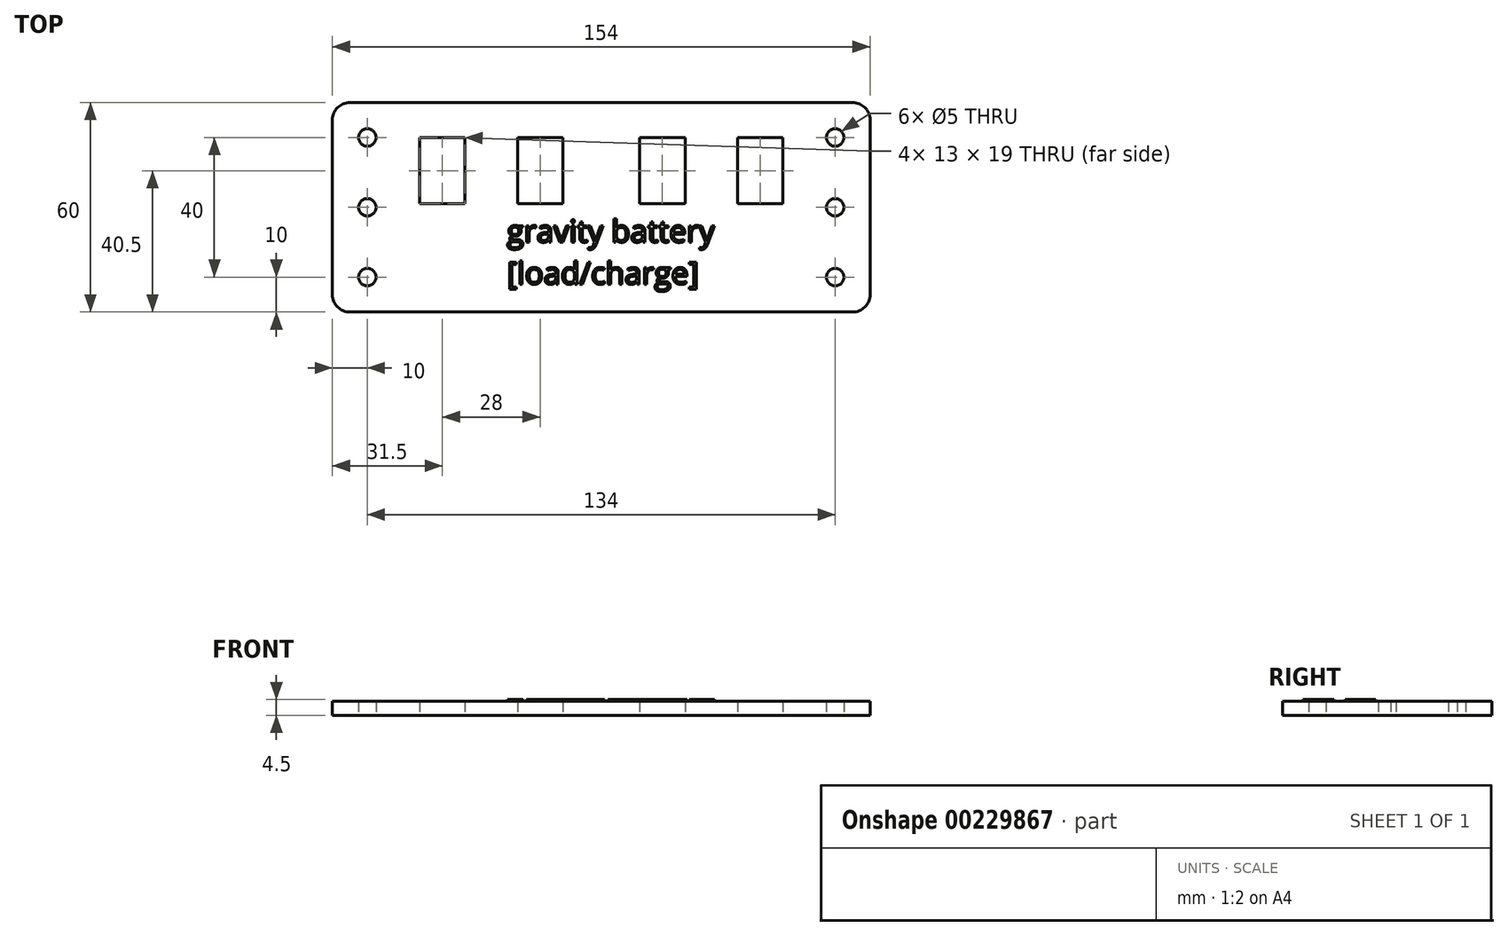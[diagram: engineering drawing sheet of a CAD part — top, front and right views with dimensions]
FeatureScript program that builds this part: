
annotation { "Feature Type Name" : "Feature", "Feature Type Description" : "" }
export const myFeature = defineFeature(function(context is Context, id is Id, definition is map)
    precondition{}
    {
        {
            var Q0;
            Q0=qCreatedBy(makeId("Top.planeOp"),FACE);
            var sketch = newSketch(context, id + "F0", { "sketchPlane" : qUnion([Q0])});
            skPoint(sketch, "E0", {"position": v(-0.2, -0.3) * mm});
            skLineSegment(sketch, "E1.right", {"start": v(-77.2, -10.3) * mm, "end": v(-77.2, 9.7) * mm});
            skLineSegment(sketch, "E2.right", {"start": v(76.8, 9.7) * mm, "end": v(76.8, -10.3) * mm});
            skPoint(sketch, "E3", {"position": v(-67.2, -0.3) * mm});
            skPoint(sketch, "E3.positionSnap0", {"position": v(-57.2, 0.7) * mm});
            skPoint(sketch, "E3.positionSnap1", {"position": v(-67.2, 9.7) * mm});
            skPoint(sketch, "E4", {"position": v(66.8, -0.3) * mm});
            skPoint(sketch, "E4.positionSnap0", {"position": v(56.8, -0.3) * mm});
            skPoint(sketch, "E4.positionSnap1", {"position": v(66.8, 9.7) * mm});
            skCircle(sketch, "E5", {"center": v(-67.2, -0.3) * mm, "radius": 2.5 * mm});
            skCircle(sketch, "E6", {"center": v(66.8, -0.3) * mm, "radius": 2.5 * mm});
            skLineSegment(sketch, "E7.top", {"start": v(-72.2, 29.7) * mm, "end": v(-62.2, 29.7) * mm});
            skLineSegment(sketch, "E7.left", {"start": v(-77.2, 9.7) * mm, "end": v(-77.2, 24.7) * mm});
            skLineSegment(sketch, "E8.top", {"start": v(-72.2, -30.3) * mm, "end": v(-62.2, -30.3) * mm});
            skLineSegment(sketch, "E8.left", {"start": v(-77.2, -10.3) * mm, "end": v(-77.2, -25.3) * mm});
            skLineSegment(sketch, "E9.top", {"start": v(61.8, 29.7) * mm, "end": v(71.8, 29.7) * mm});
            skLineSegment(sketch, "E9.right", {"start": v(76.8, 9.7) * mm, "end": v(76.8, 24.7) * mm});
            skLineSegment(sketch, "E10.top", {"start": v(61.8, -30.3) * mm, "end": v(71.8, -30.3) * mm});
            skLineSegment(sketch, "E10.right", {"start": v(76.8, -10.3) * mm, "end": v(76.8, -25.3) * mm});
            skPoint(sketch, "E11.positionSnap0", {"position": v(-52.2, 19.7) * mm});
            skPoint(sketch, "E11.positionSnap1", {"position": v(-64.7, 29.7) * mm});
            skPoint(sketch, "E12", {"position": v(66.8, 19.7) * mm});
            skPoint(sketch, "E12.positionSnap0", {"position": v(66.8, 29.7) * mm});
            skPoint(sketch, "E12.positionSnap1", {"position": v(76.8, 19.7) * mm});
            skPoint(sketch, "E13", {"position": v(66.8, -20.3) * mm});
            skPoint(sketch, "E13.positionSnap0", {"position": v(76.8, -20.3) * mm});
            skPoint(sketch, "E13.positionSnap1", {"position": v(66.8, -30.3) * mm});
            skPoint(sketch, "E14", {"position": v(-67.2, -20.3) * mm});
            skPoint(sketch, "E14.positionSnap0", {"position": v(-77.2, -20.3) * mm});
            skPoint(sketch, "E14.positionSnap1", {"position": v(-67.2, -30.3) * mm});
            skCircle(sketch, "E15", {"center": v(66.8, 19.7) * mm, "radius": 2.5 * mm});
            skCircle(sketch, "E16", {"center": v(66.8, -20.3) * mm, "radius": 2.5 * mm});
            skCircle(sketch, "E17", {"center": v(-67.2, -20.3) * mm, "radius": 2.5 * mm});
            skPoint(sketch, "E18.visualSharp", {"position": v(-52.2, 9.7) * mm});
            skPoint(sketch, "E19.visualSharp", {"position": v(-57.2, -38.58) * mm});
            skPoint(sketch, "E20.visualSharp", {"position": v(2.8, -10.3) * mm});
            skPoint(sketch, "E21.visualSharp", {"position": v(56.8, 9.7) * mm});
            skPoint(sketch, "E22.visualSharp", {"position": v(56.8, 29.7) * mm});
            skPoint(sketch, "E23.visualSharp", {"position": v(76.8, 29.7) * mm});
            skArc(sketch, "E23.filletArc", {"start": v(76.8, 24.7) * mm, "mid": v(75.34, 28.24) * mm, "end": v(71.8, 29.7) * mm});
            skPoint(sketch, "E24.visualSharp", {"position": v(56.8, -30.3) * mm});
            skPoint(sketch, "E25.visualSharp", {"position": v(76.8, -30.3) * mm});
            skArc(sketch, "E25.filletArc", {"start": v(71.8, -30.3) * mm, "mid": v(75.34, -28.84) * mm, "end": v(76.8, -25.3) * mm});
            skPoint(sketch, "E26.visualSharp", {"position": v(-57.2, -30.3) * mm});
            skPoint(sketch, "E27.visualSharp", {"position": v(-77.2, -30.3) * mm});
            skArc(sketch, "E27.filletArc", {"start": v(-77.2, -25.3) * mm, "mid": v(-75.74, -28.84) * mm, "end": v(-72.2, -30.3) * mm});
            skPoint(sketch, "E28.visualSharp", {"position": v(-77.2, 29.7) * mm});
            skArc(sketch, "E28.filletArc", {"start": v(-72.2, 29.7) * mm, "mid": v(-75.74, 28.24) * mm, "end": v(-77.2, 24.7) * mm});
            skPoint(sketch, "E29.visualSharp", {"position": v(-52.2, 29.7) * mm});
            skLineSegment(sketch, "E30.left", {"start": v(-77.2, 24.7) * mm, "end": v(-77.2, -20.3) * mm});
            skLineSegment(sketch, "E31.left", {"start": v(76.8, 24.7) * mm, "end": v(76.8, -25.3) * mm});
            skLineSegment(sketch, "E32", {"start": v(-62.2, 29.7) * mm, "end": v(61.8, 29.7) * mm});
            skLineSegment(sketch, "E33", {"start": v(-62.2, -30.3) * mm, "end": v(61.8, -30.3) * mm});
            skLineSegment(sketch, "E34.bottom", {"start": v(-52.2, 19.7) * mm, "end": v(-39.2, 19.7) * mm});
            skLineSegment(sketch, "E34.top", {"start": v(-52.2, 0.7) * mm, "end": v(-39.2, 0.7) * mm});
            skLineSegment(sketch, "E34.left", {"start": v(-52.2, 19.7) * mm, "end": v(-52.2, 0.7) * mm});
            skLineSegment(sketch, "E34.right", {"start": v(-39.2, 19.7) * mm, "end": v(-39.2, 0.7) * mm});
            skLineSegment(sketch, "E35.bottom", {"start": v(-24.2, 19.7) * mm, "end": v(-11.2, 19.7) * mm});
            skLineSegment(sketch, "E35.top", {"start": v(-24.2, 0.7) * mm, "end": v(-11.2, 0.7) * mm});
            skLineSegment(sketch, "E35.left", {"start": v(-24.2, 19.7) * mm, "end": v(-24.2, 0.7) * mm});
            skLineSegment(sketch, "E35.right", {"start": v(-11.2, 19.7) * mm, "end": v(-11.2, 0.7) * mm});
            skLineSegment(sketch, "E36.bottom", {"start": v(10.8, 19.7) * mm, "end": v(23.8, 19.7) * mm});
            skLineSegment(sketch, "E36.top", {"start": v(10.8, 0.7) * mm, "end": v(23.8, 0.7) * mm});
            skLineSegment(sketch, "E36.left", {"start": v(10.8, 19.7) * mm, "end": v(10.8, 0.7) * mm});
            skLineSegment(sketch, "E36.right", {"start": v(23.8, 19.7) * mm, "end": v(23.8, 0.7) * mm});
            skLineSegment(sketch, "E37.bottom", {"start": v(38.8, 19.7) * mm, "end": v(51.8, 19.7) * mm});
            skLineSegment(sketch, "E37.top", {"start": v(38.8, 0.7) * mm, "end": v(51.8, 0.7) * mm});
            skLineSegment(sketch, "E37.left", {"start": v(38.8, 19.7) * mm, "end": v(38.8, 0.7) * mm});
            skLineSegment(sketch, "E37.right", {"start": v(51.8, 19.7) * mm, "end": v(51.8, 0.7) * mm});
            skCircle(sketch, "E38", {"center": v(-67.2, 19.7) * mm, "radius": 2.5 * mm});
            skLineSegment(sketch, "E39", {"start": v(-57.2, 0.7) * mm, "end": v(-57.2, -38.58) * mm, "construction": true});
            skPoint(sketch, "E40", {"position": v(-57.2, -18.94) * mm});
            skLineSegment(sketch, "E41.left", {"start": v(-57.2, -18.94) * mm, "end": v(-57.2, -25.3) * mm});
            skLineSegment(sketch, "E41.right", {"start": v(2.8, -18.94) * mm, "end": v(2.8, -25.3) * mm});
            skText(sketch, "E42", { "text": "gravity battery \n[load/charge]", "fontName": "OpenSans-Regular.ttf"});
            skLineSegment(sketch, "E43.0", {"start": v(-54.2, 21.7) * mm, "end": v(-37.2, 21.7) * mm});
            skLineSegment(sketch, "E43.1", {"start": v(-54.2, 21.7) * mm, "end": v(-54.2, -1.3) * mm});
            skLineSegment(sketch, "E43.2", {"start": v(-54.2, -1.3) * mm, "end": v(-37.2, -1.3) * mm});
            skLineSegment(sketch, "E43.3", {"start": v(-37.2, 21.7) * mm, "end": v(-37.2, -1.3) * mm});
            skLineSegment(sketch, "E44.0", {"start": v(-26.2, 21.7) * mm, "end": v(-9.2, 21.7) * mm});
            skLineSegment(sketch, "E44.1", {"start": v(-26.2, 21.7) * mm, "end": v(-26.2, -1.3) * mm});
            skLineSegment(sketch, "E44.2", {"start": v(-26.2, -1.3) * mm, "end": v(-9.2, -1.3) * mm});
            skLineSegment(sketch, "E44.3", {"start": v(-9.2, 21.7) * mm, "end": v(-9.2, -1.3) * mm});
            skLineSegment(sketch, "E45.0", {"start": v(25.8, 21.7) * mm, "end": v(25.8, -1.3) * mm});
            skLineSegment(sketch, "E45.1", {"start": v(8.8, 21.7) * mm, "end": v(25.8, 21.7) * mm});
            skLineSegment(sketch, "E45.2", {"start": v(8.8, 21.7) * mm, "end": v(8.8, -1.3) * mm});
            skLineSegment(sketch, "E45.3", {"start": v(8.8, -1.3) * mm, "end": v(25.8, -1.3) * mm});
            skLineSegment(sketch, "E46.0", {"start": v(36.8, 21.7) * mm, "end": v(36.8, -1.3) * mm});
            skLineSegment(sketch, "E46.1", {"start": v(36.8, 21.7) * mm, "end": v(53.8, 21.7) * mm});
            skLineSegment(sketch, "E46.2", {"start": v(53.8, 21.7) * mm, "end": v(53.8, -1.3) * mm});
            skLineSegment(sketch, "E46.3", {"start": v(36.8, -1.3) * mm, "end": v(53.8, -1.3) * mm});
            const initialGuessF0  = {"E42": [-0.0272, -0.0103, 1, 0, 0.00636]};
            skSetInitialGuess(sketch, initialGuessF0);
            skSolve(sketch);
        }
        {
            var Q0;
            Q0=makeQuery(id+"F0.imprint","IMPRINT",FACE,{"disambiguationData":[TD([[makeQuery(id+"F0.imprint","IMPRINT",EDGE,{"derivedFrom":sQuery(id+"F0.wireOp",EDGE,"E5")}),-1.0]])]});
            var Q1;
            Q1=makeQuery(id+"F0.imprint","IMPRINT",FACE,{"disambiguationData":[TD([[makeQuery(id+"F0.imprint","IMPRINT",EDGE,{"derivedFrom":sQuery(id+"F0.wireOp",EDGE,"E34.bottom")}),1.0]])]});
            var Q2;
            Q2=makeQuery(id+"F0.imprint","IMPRINT",FACE,{"disambiguationData":[TD([[makeQuery(id+"F0.imprint","IMPRINT",EDGE,{"derivedFrom":sQuery(id+"F0.wireOp",EDGE,"E35.bottom")}),1.0]])]});
            var Q3;
            Q3=makeQuery(id+"F0.imprint","IMPRINT",FACE,{"disambiguationData":[TD([[makeQuery(id+"F0.imprint","IMPRINT",EDGE,{"derivedFrom":sQuery(id+"F0.wireOp",EDGE,"E36.bottom")}),1.0]])]});
            var Q4;
            Q4=makeQuery(id+"F0.imprint","IMPRINT",FACE,{"disambiguationData":[TD([[makeQuery(id+"F0.imprint","IMPRINT",EDGE,{"derivedFrom":sQuery(id+"F0.wireOp",EDGE,"E37.bottom")}),1.0]])]});
            extrude(context, id + "F1", {"entities" : qUnion([Q0, Q1, Q2, Q3, Q4]), "depth" : 4 * mm});
        }
        {
            var Q0;
            Q0=makeQuery(id+"F0.imprint","IMPRINT",FACE,{"disambiguationData":[TD([[makeQuery(id+"F0.imprint","IMPRINT",EDGE,{"derivedFrom":sQuery(id+"F0.wireOp",EDGE,"E42.sketch_text.stroke-285")}),-1.0]])]});
            var Q1;
            Q1=makeQuery(id+"F0.imprint","IMPRINT",FACE,{"disambiguationData":[TD([[makeQuery(id+"F0.imprint","IMPRINT",EDGE,{"derivedFrom":sQuery(id+"F0.wireOp",EDGE,"E42.sketch_text.stroke-277")}),-1.0]])]});
            var Q2;
            Q2=makeQuery(id+"F0.imprint","IMPRINT",FACE,{"disambiguationData":[TD([[makeQuery(id+"F0.imprint","IMPRINT",EDGE,{"derivedFrom":sQuery(id+"F0.wireOp",EDGE,"E42.sketch_text.stroke-289")}),-1.0]])]});
            var Q3;
            Q3=makeQuery(id+"F0.imprint","IMPRINT",FACE,{"disambiguationData":[TD([[makeQuery(id+"F0.imprint","IMPRINT",EDGE,{"derivedFrom":sQuery(id+"F0.wireOp",EDGE,"E42.sketch_text.stroke-306")}),-1.0]])]});
            var Q4;
            Q4=makeQuery(id+"F0.imprint","IMPRINT",FACE,{"disambiguationData":[TD([[makeQuery(id+"F0.imprint","IMPRINT",EDGE,{"derivedFrom":sQuery(id+"F0.wireOp",EDGE,"E42.sketch_text.stroke-333")}),-1.0]])]});
            var Q5;
            Q5=makeQuery(id+"F0.imprint","IMPRINT",FACE,{"disambiguationData":[TD([[makeQuery(id+"F0.imprint","IMPRINT",EDGE,{"derivedFrom":sQuery(id+"F0.wireOp",EDGE,"E42.sketch_text.stroke-357")}),-1.0]])]});
            var Q6;
            Q6=makeQuery(id+"F0.imprint","IMPRINT",FACE,{"disambiguationData":[TD([[makeQuery(id+"F0.imprint","IMPRINT",EDGE,{"derivedFrom":sQuery(id+"F0.wireOp",EDGE,"E42.sketch_text.stroke-361")}),-1.0]])]});
            var Q7;
            Q7=makeQuery(id+"F0.imprint","IMPRINT",FACE,{"disambiguationData":[TD([[makeQuery(id+"F0.imprint","IMPRINT",EDGE,{"derivedFrom":sQuery(id+"F0.wireOp",EDGE,"E42.sketch_text.stroke-376")}),-1.0]])]});
            var Q8;
            Q8=makeQuery(id+"F0.imprint","IMPRINT",FACE,{"disambiguationData":[TD([[makeQuery(id+"F0.imprint","IMPRINT",EDGE,{"derivedFrom":sQuery(id+"F0.wireOp",EDGE,"E42.sketch_text.stroke-394")}),-1.0]])]});
            var Q9;
            Q9=makeQuery(id+"F0.imprint","IMPRINT",FACE,{"disambiguationData":[TD([[makeQuery(id+"F0.imprint","IMPRINT",EDGE,{"derivedFrom":sQuery(id+"F0.wireOp",EDGE,"E42.sketch_text.stroke-421")}),-1.0]])]});
            var Q10;
            Q10=makeQuery(id+"F0.imprint","IMPRINT",FACE,{"disambiguationData":[TD([[makeQuery(id+"F0.imprint","IMPRINT",EDGE,{"derivedFrom":sQuery(id+"F0.wireOp",EDGE,"E42.sketch_text.stroke-434")}),-1.0]])]});
            var Q11;
            Q11=makeQuery(id+"F0.imprint","IMPRINT",FACE,{"disambiguationData":[TD([[makeQuery(id+"F0.imprint","IMPRINT",EDGE,{"derivedFrom":sQuery(id+"F0.wireOp",EDGE,"E42.sketch_text.stroke-478")}),-1.0]])]});
            var Q12;
            Q12=makeQuery(id+"F0.imprint","IMPRINT",FACE,{"disambiguationData":[TD([[makeQuery(id+"F0.imprint","IMPRINT",EDGE,{"derivedFrom":sQuery(id+"F0.wireOp",EDGE,"E42.sketch_text.stroke-497")}),-1.0]])]});
            var Q13;
            Q13=makeQuery(id+"F0.imprint","IMPRINT",FACE,{"disambiguationData":[TD([[makeQuery(id+"F0.imprint","IMPRINT",EDGE,{"derivedFrom":sQuery(id+"F0.wireOp",EDGE,"E42.sketch_text.stroke-0")}),-1.0]])]});
            var Q14;
            Q14=makeQuery(id+"F0.imprint","IMPRINT",FACE,{"disambiguationData":[TD([[makeQuery(id+"F0.imprint","IMPRINT",EDGE,{"derivedFrom":sQuery(id+"F0.wireOp",EDGE,"E42.sketch_text.stroke-44")}),-1.0]])]});
            var Q15;
            Q15=makeQuery(id+"F0.imprint","IMPRINT",FACE,{"disambiguationData":[TD([[makeQuery(id+"F0.imprint","IMPRINT",EDGE,{"derivedFrom":sQuery(id+"F0.wireOp",EDGE,"E42.sketch_text.stroke-57")}),-1.0]])]});
            var Q16;
            Q16=makeQuery(id+"F0.imprint","IMPRINT",FACE,{"disambiguationData":[TD([[makeQuery(id+"F0.imprint","IMPRINT",EDGE,{"derivedFrom":sQuery(id+"F0.wireOp",EDGE,"E42.sketch_text.stroke-84")}),-1.0]])]});
            var Q17;
            Q17=makeQuery(id+"F0.imprint","IMPRINT",FACE,{"disambiguationData":[TD([[makeQuery(id+"F0.imprint","IMPRINT",EDGE,{"derivedFrom":sQuery(id+"F0.wireOp",EDGE,"E42.sketch_text.stroke-94")}),-1.0]])]});
            var Q18;
            Q18=makeQuery(id+"F0.imprint","IMPRINT",FACE,{"disambiguationData":[TD([[makeQuery(id+"F0.imprint","IMPRINT",EDGE,{"derivedFrom":sQuery(id+"F0.wireOp",EDGE,"E42.sketch_text.stroke-98")}),-1.0]])]});
            var Q19;
            Q19=makeQuery(id+"F0.imprint","IMPRINT",FACE,{"disambiguationData":[TD([[makeQuery(id+"F0.imprint","IMPRINT",EDGE,{"derivedFrom":sQuery(id+"F0.wireOp",EDGE,"E42.sketch_text.stroke-106")}),-1.0]])]});
            var Q20;
            Q20=makeQuery(id+"F0.imprint","IMPRINT",FACE,{"disambiguationData":[TD([[makeQuery(id+"F0.imprint","IMPRINT",EDGE,{"derivedFrom":sQuery(id+"F0.wireOp",EDGE,"E42.sketch_text.stroke-125")}),-1.0]])]});
            var Q21;
            Q21=makeQuery(id+"F0.imprint","IMPRINT",FACE,{"disambiguationData":[TD([[makeQuery(id+"F0.imprint","IMPRINT",EDGE,{"derivedFrom":sQuery(id+"F0.wireOp",EDGE,"E42.sketch_text.stroke-141")}),-1.0]])]});
            var Q22;
            Q22=makeQuery(id+"F0.imprint","IMPRINT",FACE,{"disambiguationData":[TD([[makeQuery(id+"F0.imprint","IMPRINT",EDGE,{"derivedFrom":sQuery(id+"F0.wireOp",EDGE,"E42.sketch_text.stroke-164")}),-1.0]])]});
            var Q23;
            Q23=makeQuery(id+"F0.imprint","IMPRINT",FACE,{"disambiguationData":[TD([[makeQuery(id+"F0.imprint","IMPRINT",EDGE,{"derivedFrom":sQuery(id+"F0.wireOp",EDGE,"E42.sketch_text.stroke-191")}),-1.0]])]});
            var Q24;
            Q24=makeQuery(id+"F0.imprint","IMPRINT",FACE,{"disambiguationData":[TD([[makeQuery(id+"F0.imprint","IMPRINT",EDGE,{"derivedFrom":sQuery(id+"F0.wireOp",EDGE,"E42.sketch_text.stroke-210")}),-1.0]])]});
            var Q25;
            Q25=makeQuery(id+"F0.imprint","IMPRINT",FACE,{"disambiguationData":[TD([[makeQuery(id+"F0.imprint","IMPRINT",EDGE,{"derivedFrom":sQuery(id+"F0.wireOp",EDGE,"E42.sketch_text.stroke-229")}),-1.0]])]});
            var Q26;
            Q26=makeQuery(id+"F0.imprint","IMPRINT",FACE,{"disambiguationData":[TD([[makeQuery(id+"F0.imprint","IMPRINT",EDGE,{"derivedFrom":sQuery(id+"F0.wireOp",EDGE,"E42.sketch_text.stroke-248")}),-1.0]])]});
            var Q27;
            Q27=makeQuery(id+"F0.imprint","IMPRINT",FACE,{"disambiguationData":[TD([[makeQuery(id+"F0.imprint","IMPRINT",EDGE,{"derivedFrom":sQuery(id+"F0.wireOp",EDGE,"E42.sketch_text.stroke-261")}),-1.0]])]});
            extrude(context, id + "F2", {"entities" : qUnion([Q0, Q1, Q2, Q3, Q4, Q5, Q6, Q7, Q8, Q9, Q10, Q11, Q12, Q13, Q14, Q15, Q16, Q17, Q18, Q19, Q20, Q21, Q22, Q23, Q24, Q25, Q26, Q27]), "operationType" : NewBodyOperationType.ADD, "depth" : 4.5 * mm});
        }
        {
            var Q0;
            Q0=makeQuery(id+"F0.imprint","IMPRINT",FACE,{"disambiguationData":[TD([[makeQuery(id+"F0.imprint","IMPRINT",EDGE,{"derivedFrom":sQuery(id+"F0.wireOp",EDGE,"E42.sketch_text.stroke-29")}),1.0]])]});
            var Q1;
            Q1=makeQuery(id+"F0.imprint","IMPRINT",FACE,{"disambiguationData":[TD([[makeQuery(id+"F0.imprint","IMPRINT",EDGE,{"derivedFrom":sQuery(id+"F0.wireOp",EDGE,"E42.sketch_text.stroke-38")}),1.0]])]});
            var Q2;
            Q2=makeQuery(id+"F0.imprint","IMPRINT",FACE,{"disambiguationData":[TD([[makeQuery(id+"F0.imprint","IMPRINT",EDGE,{"derivedFrom":sQuery(id+"F0.wireOp",EDGE,"E42.sketch_text.stroke-76")}),1.0]])]});
            var Q3;
            Q3=makeQuery(id+"F0.imprint","IMPRINT",FACE,{"disambiguationData":[TD([[makeQuery(id+"F0.imprint","IMPRINT",EDGE,{"derivedFrom":sQuery(id+"F0.wireOp",EDGE,"E42.sketch_text.stroke-298")}),1.0]])]});
            var Q4;
            Q4=makeQuery(id+"F0.imprint","IMPRINT",FACE,{"disambiguationData":[TD([[makeQuery(id+"F0.imprint","IMPRINT",EDGE,{"derivedFrom":sQuery(id+"F0.wireOp",EDGE,"E42.sketch_text.stroke-325")}),1.0]])]});
            var Q5;
            Q5=makeQuery(id+"F0.imprint","IMPRINT",FACE,{"disambiguationData":[TD([[makeQuery(id+"F0.imprint","IMPRINT",EDGE,{"derivedFrom":sQuery(id+"F0.wireOp",EDGE,"E42.sketch_text.stroke-348")}),1.0]])]});
            var Q6;
            Q6=makeQuery(id+"F0.imprint","IMPRINT",FACE,{"disambiguationData":[TD([[makeQuery(id+"F0.imprint","IMPRINT",EDGE,{"derivedFrom":sQuery(id+"F0.wireOp",EDGE,"E42.sketch_text.stroke-156")}),1.0]])]});
            var Q7;
            Q7=makeQuery(id+"F0.imprint","IMPRINT",FACE,{"disambiguationData":[TD([[makeQuery(id+"F0.imprint","IMPRINT",EDGE,{"derivedFrom":sQuery(id+"F0.wireOp",EDGE,"E42.sketch_text.stroke-183")}),1.0]])]});
            var Q8;
            Q8=makeQuery(id+"F0.imprint","IMPRINT",FACE,{"disambiguationData":[TD([[makeQuery(id+"F0.imprint","IMPRINT",EDGE,{"derivedFrom":sQuery(id+"F0.wireOp",EDGE,"E42.sketch_text.stroke-413")}),1.0]])]});
            var Q9;
            Q9=makeQuery(id+"F0.imprint","IMPRINT",FACE,{"disambiguationData":[TD([[makeQuery(id+"F0.imprint","IMPRINT",EDGE,{"derivedFrom":sQuery(id+"F0.wireOp",EDGE,"E42.sketch_text.stroke-472")}),1.0]])]});
            var Q10;
            Q10=makeQuery(id+"F0.imprint","IMPRINT",FACE,{"disambiguationData":[TD([[makeQuery(id+"F0.imprint","IMPRINT",EDGE,{"derivedFrom":sQuery(id+"F0.wireOp",EDGE,"E42.sketch_text.stroke-463")}),1.0]])]});
            var Q11;
            Q11=makeQuery(id+"F0.imprint","IMPRINT",FACE,{"disambiguationData":[TD([[makeQuery(id+"F0.imprint","IMPRINT",EDGE,{"derivedFrom":sQuery(id+"F0.wireOp",EDGE,"E42.sketch_text.stroke-243")}),1.0]])]});
            var Q12;
            Q12=makeQuery(id+"F0.imprint","IMPRINT",FACE,{"disambiguationData":[TD([[makeQuery(id+"F0.imprint","IMPRINT",EDGE,{"derivedFrom":sQuery(id+"F0.wireOp",EDGE,"E42.sketch_text.stroke-492")}),1.0]])]});
            extrude(context, id + "F3", {"entities" : qUnion([Q0, Q1, Q2, Q3, Q4, Q5, Q6, Q7, Q8, Q9, Q10, Q11, Q12]), "operationType" : NewBodyOperationType.ADD, "depth" : 4 * mm});
        }
    });
